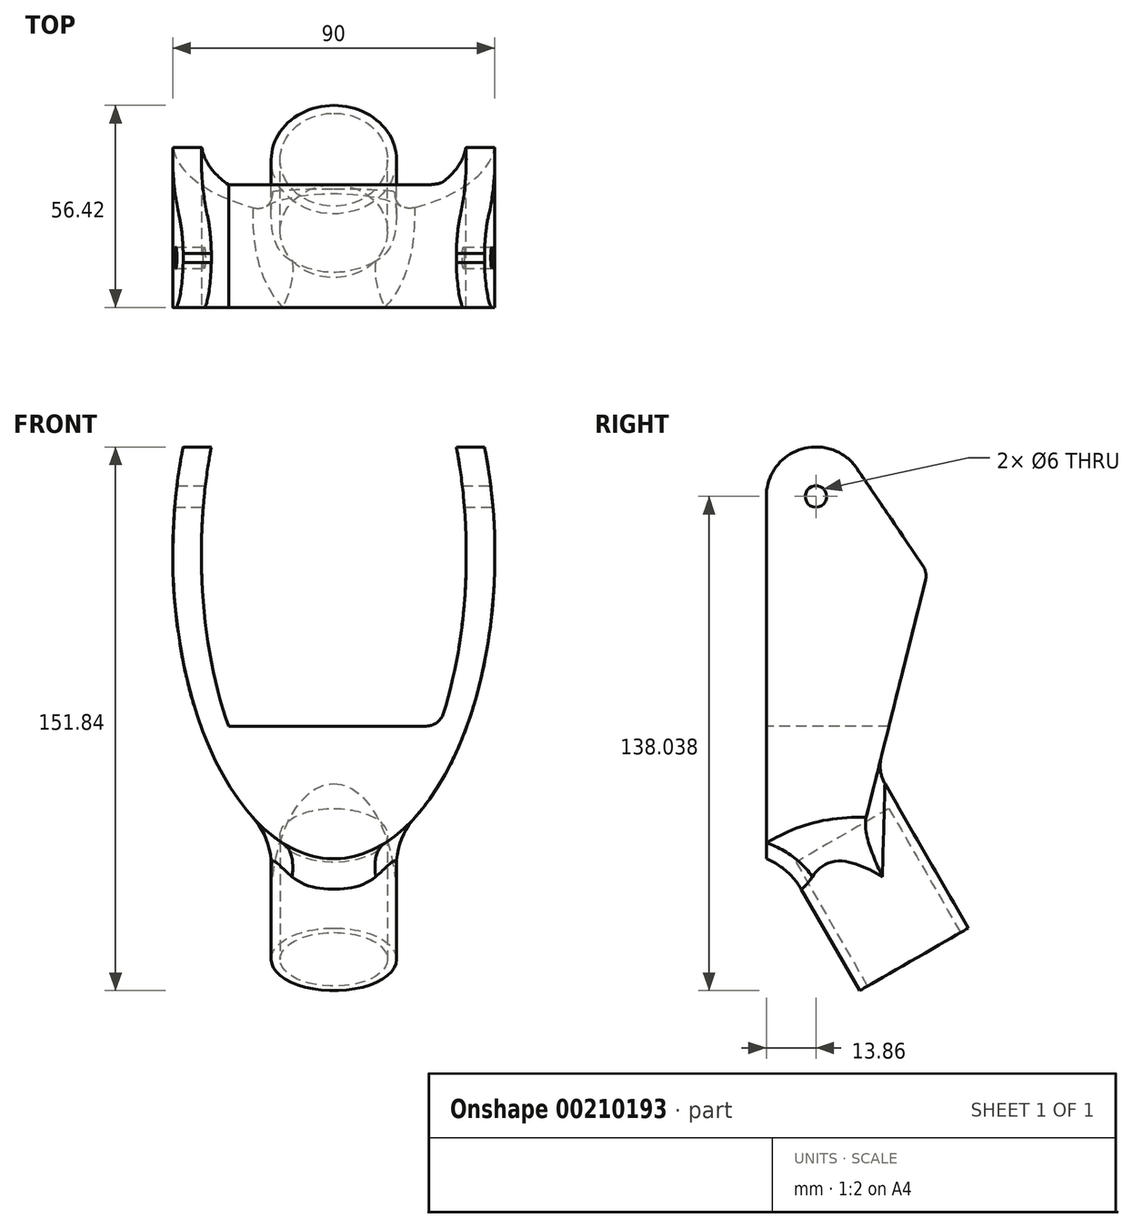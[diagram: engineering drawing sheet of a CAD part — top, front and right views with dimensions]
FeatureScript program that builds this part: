
annotation { "Feature Type Name" : "Feature", "Feature Type Description" : "" }
export const myFeature = defineFeature(function(context is Context, id is Id, definition is map)
    precondition{}
    {
        {
            var Q0;
            Q0=qCreatedBy(makeId("Front.planeOp"),FACE);
            var sketch = newSketch(context, id + "F0", { "sketchPlane" : qUnion([Q0])});
            skEllipticalArc(sketch, "E0", {});
            skEllipticalArc(sketch, "E1", {});
            skLineSegment(sketch, "E2.trimOffspring", {"start": v(34.23, 30) * mm, "end": v(42.1, 30) * mm});
            skPoint(sketch, "E3.start.orphan", {"position": v(0, -85) * mm});
            skLineSegment(sketch, "E4", {"start": v(-42.1, 30) * mm, "end": v(-34.23, 30) * mm});
            const initialGuessF0  = {"E0": [0, 0, 1, 0, 0.045, 0.085, 2.7808799332262684, 0.36071272036352475], "E1": [0, 0, 0, 1, 0.079, 0.037, 1.18127371035024, 5.101911596829346]};
            skSetInitialGuess(sketch, initialGuessF0);
            skSolve(sketch);
        }
        {
            var Q0;
            Q0=makeQuery(id+"F0.imprint","IMPRINT",FACE,{"disambiguationData":[TD([[makeQuery(id+"F0.imprint","IMPRINT",EDGE,{"derivedFrom":sQuery(id+"F0.wireOp",EDGE,"E0")}),1.0]])]});
            extrude(context, id + "F1", {"entities" : qUnion([Q0]), "depth" : 45 * mm});
        }
        {
            var Q0;
            Q0=qCreatedBy(makeId("Right.planeOp"),FACE);
            var sketch = newSketch(context, id + "F2", { "sketchPlane" : qUnion([Q0])});
            skLineSegment(sketch, "E5", {"start": v(-19.67, 23.98) * mm, "end": v(-1.26, -3.15) * mm});
            skLineSegment(sketch, "E6", {"start": v(-0.54, -7.17) * mm, "end": v(-20, -85) * mm});
            skLineSegment(sketch, "E7", {"start": v(-45, 16.2) * mm, "end": v(-45, -85) * mm});
            skLineSegment(sketch, "E8", {"start": v(-45, -85) * mm, "end": v(-20, -85) * mm});
            skArc(sketch, "E9", {"start": v(-19.67, 23.98) * mm, "mid": v(-35.21, 29.45) * mm, "end": v(-45, 16.2) * mm});
            skPoint(sketch, "E9.first.point", {"position": v(-19.67, 23.98) * mm});
            skPoint(sketch, "E9.second.point", {"position": v(-29.87, 30) * mm});
            skPoint(sketch, "E9.third.point", {"position": v(-45, 16.2) * mm});
            skPoint(sketch, "E10.visualSharp", {"position": v(0, -5) * mm});
            skArc(sketch, "E10.filletArc", {"start": v(-0.54, -7.17) * mm, "mid": v(-0.47, -5.08) * mm, "end": v(-1.26, -3.15) * mm});
            skLineSegment(sketch, "E11.bottom", {"start": v(-93.24, 81.08) * mm, "end": v(58.8, 81.08) * mm});
            skLineSegment(sketch, "E11.top", {"start": v(-93.24, -101.08) * mm, "end": v(58.8, -101.08) * mm});
            skLineSegment(sketch, "E11.left", {"start": v(-93.24, 81.08) * mm, "end": v(-93.24, -101.08) * mm});
            skLineSegment(sketch, "E11.right", {"start": v(58.8, 81.08) * mm, "end": v(58.8, -101.08) * mm});
            skCircle(sketch, "E12", {"center": v(-31.14, 16.2) * mm, "radius": 3 * mm});
            skSolve(sketch);
        }
        {
            var Q0;
            Q0=makeQuery(id+"F2.imprint","IMPRINT",FACE,{"disambiguationData":[TD([[makeQuery(id+"F2.imprint","IMPRINT",EDGE,{"derivedFrom":sQuery(id+"F2.wireOp",EDGE,"E5")}),1.0]])]});
            var Q1;
            Q1=makeQuery(id+"F2.imprint","IMPRINT",FACE,{"disambiguationData":[TD([[makeQuery(id+"F2.imprint","IMPRINT",EDGE,{"derivedFrom":sQuery(id+"F2.wireOp",EDGE,"E12")}),1.0]])]});
            extrude(context, id + "F3", {"entities" : qUnion([Q0, Q1]), "operationType" : NewBodyOperationType.REMOVE, "endBound" : BoundingType.SYMMETRIC, "oppositeDirection" : true, "depth" : 142 * mm});
        }
        {
            var Q0;
            Q0=qCreatedBy(makeId("Right.planeOp"),FACE);
            var sketch = newSketch(context, id + "F4", { "sketchPlane" : qUnion([Q0])});
            skLineSegment(sketch, "E13", {"start": v(-19.99, -84.95) * mm, "end": v(8.12, -133.63) * mm});
            skSolve(sketch);
        }
        {
            var Q0;
            Q0=sQuery(id+"F4.wireOp",EDGE,"E13");
            var Q1;
            Q1=sQuery(id+"F4.wireOp",VERTEX,"E13.start");
            cPlane(context, id + "F5", {"entities" : qUnion([Q0, Q1]), "cplaneType" : CPlaneType.CURVE_POINT, "offset" : 25 * mm, "width" : 150 * mm, "height" : 150 * mm});
        }
        {
            var Q0;
            Q0=qCreatedBy(id+"F5.planeOp",FACE);
            var sketch = newSketch(context, id + "F6", { "sketchPlane" : qUnion([Q0])});
            skCircle(sketch, "E14", {"center": v(0, 59.79) * mm, "radius": 17.5 * mm});
            skSolve(sketch);
        }
        {
            var Q0;
            Q0=makeQuery(id+"F6.imprint","IMPRINT",FACE,{"disambiguationData":[TD([[makeQuery(id+"F6.imprint","IMPRINT",EDGE,{"derivedFrom":sQuery(id+"F6.wireOp",EDGE,"E14")}),1.0]])]});
            var Q1;
            Q1=makeQuery(id+"F1.opExtrude","SWEPT_FACE",FACE,{"disambiguationData":[OSD([sQuery(id+"F0.wireOp",EDGE,"E0")])]});
            var Q2;
            Q2=makeQuery(id+"F1.opExtrude","SWEPT_BODY",BODY,{"disambiguationData":[OSD([sQuery(id+"F0.wireOp",EDGE,"E0"),sQuery(id+"F0.wireOp",EDGE,"E1"),sQuery(id+"F0.wireOp",EDGE,"E2.trimOffspring"),sQuery(id+"F0.wireOp",EDGE,"E4")])]});
            extrude(context, id + "F7", {"entities" : qUnion([Q0]), "operationType" : NewBodyOperationType.ADD, "endBound" : BoundingType.SYMMETRIC, "oppositeDirection" : true, "endBoundEntityFace" : qUnion([Q1]), "endBoundEntityBody" : qUnion([Q2]), "depth" : 65 * mm});
        }
        {
            var Q0;
            Q0=makeQuery(id+"F1.opExtrude","CAP_FACE",FACE,{"disambiguationData":[OSD([sQuery(id+"F0.wireOp",EDGE,"E0"),sQuery(id+"F0.wireOp",EDGE,"E1"),sQuery(id+"F0.wireOp",EDGE,"E2.trimOffspring"),sQuery(id+"F0.wireOp",EDGE,"E4")])],"isStart":false});
            var sketch = newSketch(context, id + "F8", { "sketchPlane" : qUnion([Q0])});
            skLineSegment(sketch, "E15.bottom", {"start": v(-31.42, -47.95) * mm, "end": v(30.71, -47.95) * mm});
            skLineSegment(sketch, "E16", {"start": v(-31.42, -47.95) * mm, "end": v(-25.74, -62.45) * mm});
            skLineSegment(sketch, "E17", {"start": v(-25.74, -62.45) * mm, "end": v(-17.41, -73.68) * mm});
            skLineSegment(sketch, "E18", {"start": v(-17.41, -73.68) * mm, "end": v(0, -82.59) * mm});
            skLineSegment(sketch, "E19", {"start": v(0, -82.59) * mm, "end": v(13.37, -77.17) * mm});
            skLineSegment(sketch, "E20", {"start": v(13.37, -77.17) * mm, "end": v(26.92, -62.45) * mm});
            skLineSegment(sketch, "E21", {"start": v(26.92, -62.45) * mm, "end": v(30.71, -47.95) * mm});
            skSolve(sketch);
        }
        {
            var Q0;
            {var subQ0=sQuery(id+"F8.wireOp",EDGE,"E15.bottom");var subQ1=makeQuery(id+"F1.opExtrude","CAP_EDGE",EDGE,{"disambiguationData":[OSD([sQuery(id+"F0.wireOp",EDGE,"E1")])],"isStart":false});var subQ2=makeQuery(id+"F8.imprint","INTERSECT",VERTEX,{"disambiguationData":[OD(0.0)],"derivedFrom":[subQ1,subQ0]});Q0=makeQuery(id+"F8.imprint","IMPRINT",FACE,{"disambiguationData":[TD([[makeQuery(id+"F8.imprint","IMPRINT",EDGE,{"disambiguationData":[TD([[subQ2,-1.0]])],"derivedFrom":subQ0}),-1.0]])]});}
            var Q1;
            Q1=makeQuery(id+"F7.boolean.opBoolean","SPLIT",FACE,{"disambiguationData":[TD([makeQuery(id+"F3.boolean.opBoolean","COPY",FACE,{"disambiguationData":[OD(1.0)],"derivedFrom":makeQuery(id+"F3.opExtrude","SWEPT_FACE",FACE,{"disambiguationData":[OSD([sQuery(id+"F2.wireOp",EDGE,"E10.filletArc")])]})})])],"derivedFrom":makeQuery(id+"F3.boolean.opBoolean","COPY",FACE,{"derivedFrom":makeQuery(id+"F3.opExtrude","SWEPT_FACE",FACE,{"disambiguationData":[OSD([sQuery(id+"F2.wireOp",EDGE,"E6")])]})})});
            extrude(context, id + "F9", {"entities" : qUnion([Q0]), "operationType" : NewBodyOperationType.ADD, "endBound" : BoundingType.UP_TO_SURFACE, "oppositeDirection" : true, "endBoundEntityFace" : qUnion([Q1]), "depth" : 25 * mm});
        }
        {
            var Q0;
            Q0=qCreatedBy(makeId("Right.planeOp"),FACE);
            var sketch = newSketch(context, id + "F10", { "sketchPlane" : qUnion([Q0])});
            skLineSegment(sketch, "E22.bottom", {"start": v(-45, -10.32) * mm, "end": v(-91.51, -10.32) * mm});
            skLineSegment(sketch, "E22.top", {"start": v(-45, -96.95) * mm, "end": v(-91.51, -96.95) * mm});
            skLineSegment(sketch, "E22.left", {"start": v(-45, -10.32) * mm, "end": v(-45, -96.95) * mm});
            skLineSegment(sketch, "E22.right", {"start": v(-91.51, -10.32) * mm, "end": v(-91.51, -96.95) * mm});
            skSolve(sketch);
        }
        {
            var Q0;
            Q0=makeQuery(id+"F10.imprint","IMPRINT",FACE,{"disambiguationData":[TD([[makeQuery(id+"F10.imprint","IMPRINT",EDGE,{"derivedFrom":sQuery(id+"F10.wireOp",EDGE,"E22.bottom")}),1.0]])]});
            extrude(context, id + "F11", {"entities" : qUnion([Q0]), "operationType" : NewBodyOperationType.REMOVE, "endBound" : BoundingType.SYMMETRIC, "oppositeDirection" : true, "depth" : 42 * mm});
        }
        {
            var Q0;
            Q0=makeQuery(id+"F9.boolean.opBoolean","INTERSECT",EDGE,{"derivedFrom":[makeQuery(id+"F7.opExtrude","SWEPT_FACE",FACE,{"disambiguationData":[OSD([sQuery(id+"F6.wireOp",EDGE,"E14")])]}),makeQuery(id+"F9.opExtrude","CAP_FACE",FACE,{"disambiguationData":[OSD([sQuery(id+"F0.wireOp",EDGE,"E1"),sQuery(id+"F8.wireOp",EDGE,"E15.bottom")])],"isStart":false})]});
            fillet(context, id + "F12", {"entities" : qUnion([Q0]), "radius" : 10 * mm, "tangentPropagation" : true, "allowEdgeOverflow" : false});
        }
        {
            var Q0;
            Q0=makeQuery(id+"F7.opExtrude","CAP_FACE",FACE,{"disambiguationData":[OSD([sQuery(id+"F6.wireOp",EDGE,"E14")])],"isStart":true});
            var sketch = newSketch(context, id + "F13", { "sketchPlane" : qUnion([Q0])});
            skCircle(sketch, "E23", {"center": v(0, 59.79) * mm, "radius": 15 * mm});
            skSolve(sketch);
        }
        {
            var Q0;
            Q0 = qSketchRegion(id + "F13", true);
            extrude(context, id + "F14", {"entities" : qUnion([Q0]), "operationType" : NewBodyOperationType.REMOVE, "oppositeDirection" : true, "depth" : 40 * mm});
        }
        {
            var Q0;
            {var subQ0=sQuery(id+"F8.wireOp",EDGE,"E15.bottom");var subQ1=sQuery(id+"F0.wireOp",EDGE,"E1");Q0=makeQuery(id+"F9.opExtrude","SWEPT_EDGE",EDGE,{"disambiguationData":[OSD([subQ1,subQ0]),TDD([makeQuery(id+"F8.imprint","INTERSECT",VERTEX,{"disambiguationData":[OD(1.0)],"derivedFrom":[makeQuery(id+"F1.opExtrude","CAP_EDGE",EDGE,{"disambiguationData":[OSD([subQ1])],"isStart":false}),subQ0]})])]});}
            var Q1;
            {var subQ0=sQuery(id+"F8.wireOp",EDGE,"E15.bottom");var subQ1=sQuery(id+"F0.wireOp",EDGE,"E1");Q1=makeQuery(id+"F9.opExtrude","SWEPT_EDGE",EDGE,{"disambiguationData":[OSD([subQ1,subQ0]),TDD([makeQuery(id+"F8.imprint","INTERSECT",VERTEX,{"disambiguationData":[OD(0.0)],"derivedFrom":[makeQuery(id+"F1.opExtrude","CAP_EDGE",EDGE,{"disambiguationData":[OSD([subQ1])],"isStart":false}),subQ0]})])]});}
            fillet(context, id + "F15", {"entities" : qUnion([Q0, Q1]), "radius" : 5 * mm, "tangentPropagation" : true, "allowEdgeOverflow" : false});
        }
        {
            var Q0;
            Q0=makeQuery(id+"F7.boolean.opBoolean","INTERSECT",EDGE,{"derivedFrom":[makeQuery(id+"F1.opExtrude","SWEPT_FACE",FACE,{"disambiguationData":[OSD([sQuery(id+"F0.wireOp",EDGE,"E0")])]}),makeQuery(id+"F7.opExtrude","SWEPT_FACE",FACE,{"disambiguationData":[OSD([sQuery(id+"F6.wireOp",EDGE,"E14")])]})]});
            fillet(context, id + "F16", {"entities" : qUnion([Q0]), "radius" : 20 * mm, "tangentPropagation" : true, "allowEdgeOverflow" : false});
        }
    });
